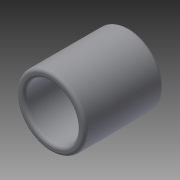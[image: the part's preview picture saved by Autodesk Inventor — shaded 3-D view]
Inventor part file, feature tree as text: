
AUTODESK INVENTOR PART (.ipt)
format: ipt  version: 2014 (Build 180170000, 170)  size: 123,392 bytes
history: native  units: in
note: dims shown in document units (in); Inventor stores cm internally (conversion verified against a paired STEP export)
features: extrude x1, fillet x1, sketch x1
ambient origin geometry x8: Origin, YZ Plane, XZ Plane, XY Plane, X Axis, Y Axis, Z Axis, Center Point
bodies: Solid1 (feature_tree)
feature tree (3):
  extrude  "Extrusion1"  Depth=0.025in
  fillet  "Fillet1"  Radius=0.6in
  sketch  "Sketch1"  dims[d0=0.525in d1=0.4in d2=0.6in d3=0.0in d4=0.025in]
